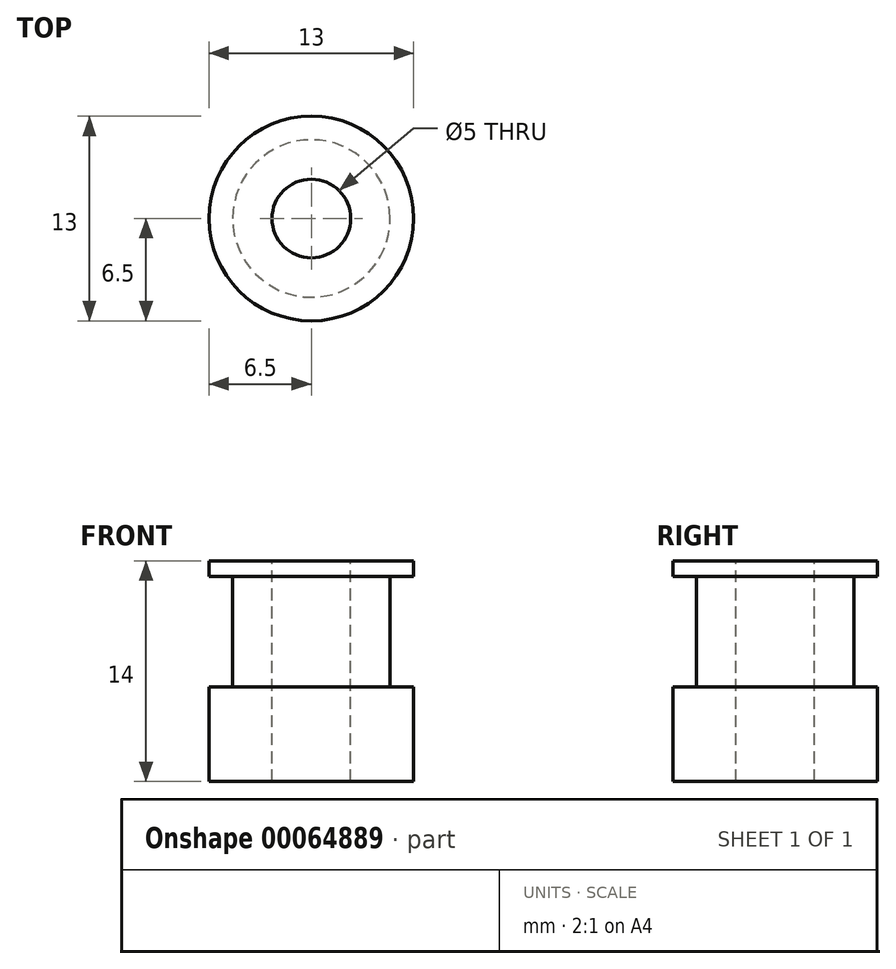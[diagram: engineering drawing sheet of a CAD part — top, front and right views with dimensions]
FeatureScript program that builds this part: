
annotation { "Feature Type Name" : "Feature", "Feature Type Description" : "" }
export const myFeature = defineFeature(function(context is Context, id is Id, definition is map)
    precondition{}
    {
        {
            var Q0;
            Q0=qCreatedBy(makeId("Top.planeOp"),FACE);
            var sketch = newSketch(context, id + "F0", { "sketchPlane" : qUnion([Q0])});
            skCircle(sketch, "E0", {"center": v(0, 0) * mm, "radius": 6.5 * mm});
            skSolve(sketch);
        }
        {
            var Q0;
            Q0=qSketchRegion(id+"F0",true);
            extrude(context, id + "F1", {"entities" : qUnion([Q0]), "depth" : 6 * mm, "offsetDistance" : 25 * mm});
        }
        {
            var Q0;
            Q0=makeQuery(id+"F1.opExtrude","CAP_FACE",FACE,{"disambiguationData":[OSD([sQuery(id+"F0.wireOp",EDGE,"E0")])],"isStart":false});
            var sketch = newSketch(context, id + "F2", { "sketchPlane" : qUnion([Q0])});
            skCircle(sketch, "E1", {"center": v(0, 0) * mm, "radius": 5 * mm});
            skSolve(sketch);
        }
        {
            var Q0;
            Q0=qSketchRegion(id+"F2",true);
            extrude(context, id + "F3", {"entities" : qUnion([Q0]), "operationType" : NewBodyOperationType.ADD, "depth" : 7 * mm, "offsetDistance" : 25 * mm});
        }
        {
            var Q0;
            Q0=makeQuery(id+"F3.opExtrude","CAP_FACE",FACE,{"disambiguationData":[OSD([sQuery(id+"F2.wireOp",EDGE,"E1")])],"isStart":false});
            var sketch = newSketch(context, id + "F4", { "sketchPlane" : qUnion([Q0])});
            skCircle(sketch, "E2", {"center": v(0, 0) * mm, "radius": 6.5 * mm});
            skSolve(sketch);
        }
        {
            var Q0;
            Q0=qSketchRegion(id+"F4",true);
            extrude(context, id + "F5", {"entities" : qUnion([Q0]), "operationType" : NewBodyOperationType.ADD, "depth" : 1 * mm, "offsetDistance" : 25 * mm});
        }
        {
            var Q0;
            Q0=makeQuery(id+"F5.opExtrude","CAP_FACE",FACE,{"disambiguationData":[OSD([sQuery(id+"F4.wireOp",EDGE,"E2")])],"isStart":false});
            var sketch = newSketch(context, id + "F6", { "sketchPlane" : qUnion([Q0])});
            skCircle(sketch, "E3", {"center": v(0, 0) * mm, "radius": 2.5 * mm});
            skSolve(sketch);
        }
        {
            var Q0;
            Q0=qSketchRegion(id+"F6",true);
            extrude(context, id + "F7", {"entities" : qUnion([Q0]), "operationType" : NewBodyOperationType.REMOVE, "oppositeDirection" : true, "depth" : 25 * mm});
        }
    });
